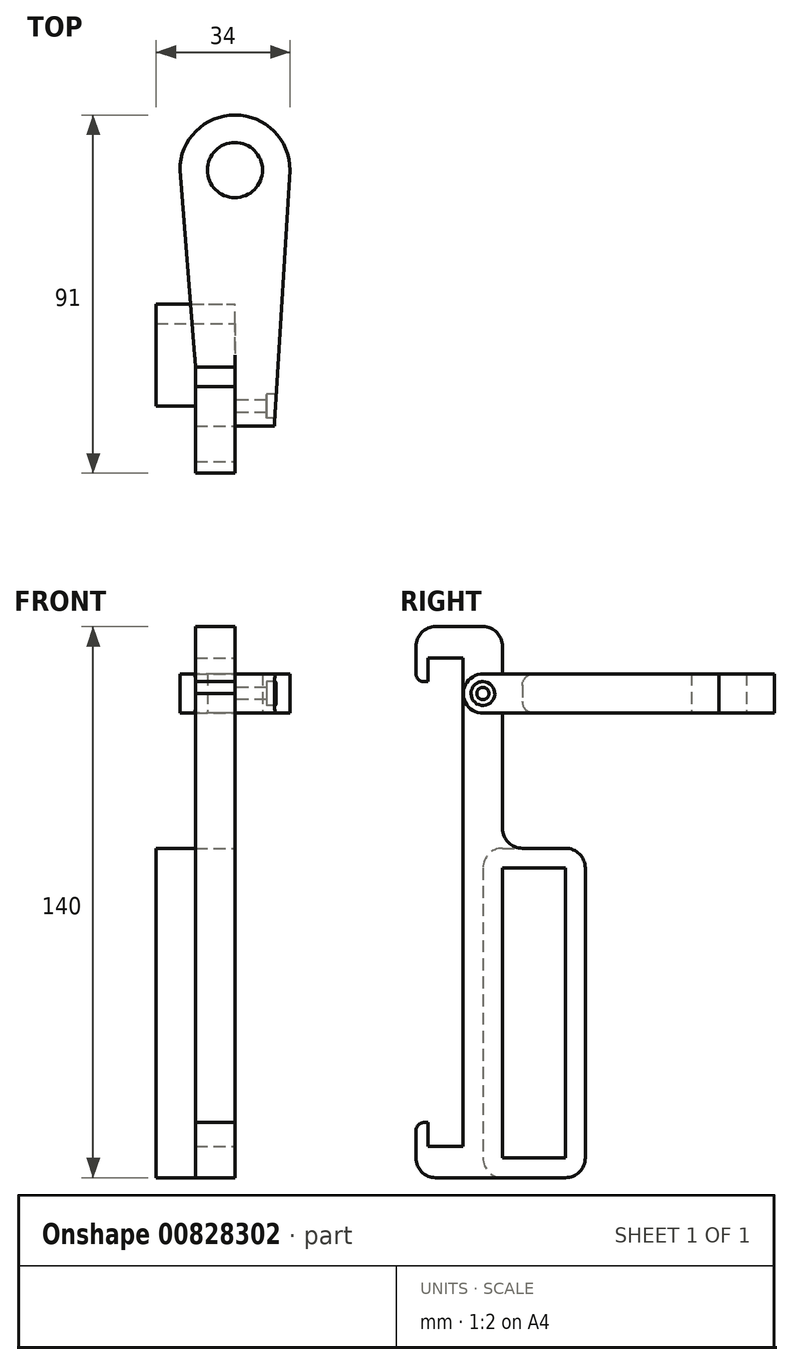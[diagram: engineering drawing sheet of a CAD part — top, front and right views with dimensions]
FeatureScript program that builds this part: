
annotation { "Feature Type Name" : "Feature", "Feature Type Description" : "" }
export const myFeature = defineFeature(function(context is Context, id is Id, definition is map)
    precondition{}
    {
        {
            var Q0;
            Q0=qCreatedBy(makeId("Top.planeOp"),FACE);
            var sketch = newSketch(context, id + "F0", { "sketchPlane" : qUnion([Q0])});
            skCircle(sketch, "E0", {"center": v(0, 0) * mm, "radius": 7 * mm});
            skArc(sketch, "E1", {"start": v(14, 0) * mm, "mid": v(0, 14) * mm, "end": v(-14, 0) * mm});
            skLineSegment(sketch, "E2", {"start": v(10, -65) * mm, "end": v(0, -65) * mm});
            skLineSegment(sketch, "E3", {"start": v(0, -65) * mm, "end": v(0, -50) * mm});
            skLineSegment(sketch, "E4", {"start": v(0, -50) * mm, "end": v(-10, -50) * mm});
            skLineSegment(sketch, "E5", {"start": v(-10, -50) * mm, "end": v(-14, 0) * mm});
            skLineSegment(sketch, "E6", {"start": v(0, 0) * mm, "end": v(0, -50) * mm, "construction": true});
            skLineSegment(sketch, "E7", {"start": v(14, 0) * mm, "end": v(10, -65) * mm});
            skSolve(sketch);
        }
        {
            var Q0;
            Q0 = qSketchRegion(id + "F0", true);
            extrude(context, id + "F1", {"entities" : qUnion([Q0]), "depth" : 10 * mm, "offsetDistance" : 25 * mm});
        }
        {
            var Q0;
            Q0=makeQuery(id+"F1.opExtrude","CAP_EDGE",EDGE,{"disambiguationData":[OSD([sQuery(id+"F0.wireOp",EDGE,"E2")])],"isStart":false});
            var Q1;
            Q1=makeQuery(id+"F1.opExtrude","CAP_EDGE",EDGE,{"disambiguationData":[OSD([sQuery(id+"F0.wireOp",EDGE,"E2")])],"isStart":true});
            fillet(context, id + "F2", {"entities" : qUnion([Q0, Q1]), "radius" : 5 * mm, "tangentPropagation" : true, "allowEdgeOverflow" : false});
        }
        {
            var Q0;
            Q0=makeQuery(id+"F1.opExtrude","SWEPT_FACE",FACE,{"disambiguationData":[OSD([sQuery(id+"F0.wireOp",EDGE,"E3")])]});
            var sketch = newSketch(context, id + "F3", { "sketchPlane" : qUnion([Q0])});
            skPoint(sketch, "E8", {"position": v(60, 0) * mm});
            skPoint(sketch, "E9", {"position": v(60, 10) * mm});
            skLineSegment(sketch, "E10", {"start": v(60, 0) * mm, "end": v(60, 10) * mm, "construction": true});
            skCircle(sketch, "E11", {"center": v(60, 5) * mm, "radius": 1.55 * mm});
            skCircle(sketch, "E12", {"center": v(60, 5) * mm, "radius": 3.05 * mm});
            skSolve(sketch);
        }
        {
            var Q0;
            Q0=makeQuery(id+"F3.imprint","IMPRINT",FACE,{"disambiguationData":[TD([[makeQuery(id+"F3.imprint","IMPRINT",EDGE,{"derivedFrom":sQuery(id+"F3.wireOp",EDGE,"E11")}),1.0]])]});
            var Q1;
            Q1=sQuery(id+"F3.wireOp",EDGE,"E11");
            var Q2;
            Q2=makeQuery(id+"F1.opExtrude","SWEPT_FACE",FACE,{"disambiguationData":[OSD([sQuery(id+"F0.wireOp",EDGE,"E7")])]});
            extrude(context, id + "F4", {"entities" : qUnion([Q0]), "operationType" : NewBodyOperationType.REMOVE, "surfaceEntities" : qUnion([Q1]), "endBound" : BoundingType.UP_TO_SURFACE, "oppositeDirection" : true, "depth" : 25 * mm, "endBoundEntityFace" : qUnion([Q2]), "offsetDistance" : 25 * mm});
        }
        {
            var Q0;
            Q0=makeQuery(id+"F3.imprint","IMPRINT",FACE,{"disambiguationData":[TD([[makeQuery(id+"F3.imprint","IMPRINT",EDGE,{"derivedFrom":sQuery(id+"F3.wireOp",EDGE,"E11")}),-1.0]])]});
            extrude(context, id + "F5", {"entities" : qUnion([Q0]), "operationType" : NewBodyOperationType.REMOVE, "oppositeDirection" : true, "depth" : 12 * mm, "offsetDistance" : 25 * mm, "hasSecondDirection" : true, "secondDirectionOppositeDirection" : true, "secondDirectionDepth" : 8 * mm});
        }
        {
            var Q0;
            Q0=makeQuery(id+"F1.opExtrude","SWEPT_FACE",FACE,{"disambiguationData":[OSD([sQuery(id+"F0.wireOp",EDGE,"E3")])]});
            var sketch = newSketch(context, id + "F6", { "sketchPlane" : qUnion([Q0])});
            skLineSegment(sketch, "E13", {"start": v(65, -110) * mm, "end": v(74, -110) * mm});
            skLineSegment(sketch, "E14", {"start": v(74, -110) * mm, "end": v(74, -104) * mm});
            skLineSegment(sketch, "E15", {"start": v(74, -104) * mm, "end": v(75, -104) * mm});
            skLineSegment(sketch, "E16", {"start": v(77, -106) * mm, "end": v(77, -113) * mm});
            skLineSegment(sketch, "E17", {"start": v(55, -110) * mm, "end": v(55, -113) * mm});
            skPoint(sketch, "E18.visualSharp", {"position": v(77, -118) * mm});
            skArc(sketch, "E18.filletArc", {"start": v(72, -118) * mm, "mid": v(75.54, -116.54) * mm, "end": v(77, -113) * mm});
            skPoint(sketch, "E19.visualSharp", {"position": v(77, -104) * mm});
            skArc(sketch, "E19.filletArc", {"start": v(77, -106) * mm, "mid": v(76.41, -104.59) * mm, "end": v(75, -104) * mm});
            skLineSegment(sketch, "E20", {"start": v(65, 14) * mm, "end": v(65, -110) * mm});
            skLineSegment(sketch, "E21", {"start": v(55, 14) * mm, "end": v(55, -29.3) * mm});
            skLineSegment(sketch, "E22", {"start": v(65, -48) * mm, "end": v(85, -48) * mm, "construction": true});
            skLineSegment(sketch, "E23.MirrorCS", {"start": v(65, 14) * mm, "end": v(74, 14) * mm});
            skLineSegment(sketch, "E24.MirrorCS", {"start": v(74, 14) * mm, "end": v(74, 8) * mm});
            skLineSegment(sketch, "E25.MirrorCS", {"start": v(74, 8) * mm, "end": v(75, 8) * mm});
            skArc(sketch, "E26.MirrorCS", {"start": v(77, 10) * mm, "mid": v(76.41, 8.59) * mm, "end": v(75, 8) * mm});
            skLineSegment(sketch, "E27.MirrorCS", {"start": v(77, 10) * mm, "end": v(77, 17) * mm});
            skArc(sketch, "E28.MirrorCS", {"start": v(72, 22) * mm, "mid": v(75.54, 20.54) * mm, "end": v(77, 17) * mm});
            skLineSegment(sketch, "E29.MirrorCS", {"start": v(72, 22) * mm, "end": v(60, 22) * mm});
            skArc(sketch, "E30.MirrorCS", {"start": v(55, 17) * mm, "mid": v(56.46, 20.54) * mm, "end": v(60, 22) * mm});
            skLineSegment(sketch, "E31.MirrorCS", {"start": v(55, 14) * mm, "end": v(55, 17) * mm});
            skLineSegment(sketch, "E32.bottom", {"start": v(55, -113) * mm, "end": v(39, -113) * mm});
            skLineSegment(sketch, "E32.top", {"start": v(55, -39.3) * mm, "end": v(39, -39.3) * mm});
            skLineSegment(sketch, "E32.left", {"start": v(55, -113) * mm, "end": v(55, -39.3) * mm});
            skLineSegment(sketch, "E32.right", {"start": v(39, -113) * mm, "end": v(39, -39.3) * mm});
            skLineSegment(sketch, "E33.1", {"start": v(34, -113) * mm, "end": v(34, -39.3) * mm});
            skLineSegment(sketch, "E33.2", {"start": v(50, -34.3) * mm, "end": v(39, -34.3) * mm});
            skLineSegment(sketch, "E34.trimOffspring", {"start": v(55, -39.3) * mm, "end": v(55, -110) * mm});
            skLineSegment(sketch, "E35", {"start": v(39, -118) * mm, "end": v(72, -118) * mm});
            skPoint(sketch, "E36.visualSharp", {"position": v(34, -118) * mm});
            skArc(sketch, "E36.filletArc", {"start": v(34, -113) * mm, "mid": v(35.46, -116.54) * mm, "end": v(39, -118) * mm});
            skPoint(sketch, "E37.visualSharp", {"position": v(34, -34.3) * mm});
            skArc(sketch, "E37.filletArc", {"start": v(39, -34.3) * mm, "mid": v(35.46, -35.76) * mm, "end": v(34, -39.3) * mm});
            skPoint(sketch, "E38.visualSharp", {"position": v(55, -34.3) * mm});
            skArc(sketch, "E38.filletArc", {"start": v(50, -34.3) * mm, "mid": v(53.54, -32.84) * mm, "end": v(55, -29.3) * mm});
            skSolve(sketch);
        }
        {
            var Q0;
            Q0=makeQuery(id+"F6.imprint","IMPRINT",FACE,{"disambiguationData":[TD([[makeQuery(id+"F6.imprint","IMPRINT",EDGE,{"derivedFrom":makeQuery(id+"F4.boolean.opBoolean","COPY",EDGE,{"derivedFrom":makeQuery(id+"F4.opExtrude","CAP_EDGE",EDGE,{"disambiguationData":[OSD([sQuery(id+"F3.wireOp",EDGE,"E11")])],"isStart":true})})}),-1.0]])]});
            var Q1;
            {var subQ7=sQuery(id+"F6.wireOp",EDGE,"0UclWwWG-CQ9r-8rmC-3t0o-oFOVJa3uRY5Y");Q1=makeQuery(id+"F6.imprint","IMPRINT",FACE,{"disambiguationData":[TD([[makeQuery(id+"F6.imprint","IMPRINT",EDGE,{"derivedFrom":subQ7}),1.0]])]});}
            var Q2;
            {var subQ8=sQuery(id+"F6.wireOp",EDGE,"E13");Q2=makeQuery(id+"F6.imprint","IMPRINT",FACE,{"disambiguationData":[TD([[makeQuery(id+"F6.imprint","IMPRINT",EDGE,{"derivedFrom":subQ8}),-1.0]])]});}
            var Q3;
            Q3=makeQuery(id+"F6.imprint","IMPRINT",FACE,{"disambiguationData":[TD([[makeQuery(id+"F6.imprint","IMPRINT",EDGE,{"derivedFrom":sQuery(id+"F6.wireOp",EDGE,"0UclWwWG-CQ9r-8rmC-3t0o-oFOVJa3uRY5Y")}),-1.0]])]});
            var Q4;
            {var subQ6=sQuery(id+"F6.wireOp",EDGE,"E23.MirrorCS");Q4=makeQuery(id+"F6.imprint","IMPRINT",FACE,{"disambiguationData":[TD([[makeQuery(id+"F6.imprint","IMPRINT",EDGE,{"derivedFrom":subQ6}),1.0]])]});}
            extrude(context, id + "F7", {"entities" : qUnion([Q0, Q1, Q2, Q3, Q4]), "depth" : 10 * mm, "offsetDistance" : 25 * mm});
        }
        {
            var Q0;
            Q0=makeQuery(id+"F7.opExtrude","CAP_FACE",FACE,{"disambiguationData":[OSD([sQuery(id+"F3.wireOp",EDGE,"E11"),sQuery(id+"F6.wireOp",EDGE,"bUPbGr09-necb-y4z6-tEju-2VODjiAXuSOo.left"),sQuery(id+"F6.wireOp",EDGE,"bUPbGr09-necb-y4z6-tEju-2VODjiAXuSOo.right"),sQuery(id+"F6.wireOp",EDGE,"55dd8d40-e183-4ee7-96f7-8d9655a16e07.filletArc"),sQuery(id+"F6.wireOp",EDGE,"86c6cade-5d1c-4868-ab3d-ae4e29603d97.filletArc"),sQuery(id+"F6.wireOp",EDGE,"E13"),sQuery(id+"F6.wireOp",EDGE,"E14"),sQuery(id+"F6.wireOp",EDGE,"E15"),sQuery(id+"F6.wireOp",EDGE,"E16"),sQuery(id+"F6.wireOp",EDGE,"E17"),sQuery(id+"F6.wireOp",EDGE,"JK7yhdwg-f7QC-nTv9-UEI6-wTwSWF0jWrCr"),sQuery(id+"F6.wireOp",EDGE,"5c3730f8-11a7-420e-9a6c-b66555e10253.filletArc"),sQuery(id+"F6.wireOp",EDGE,"E18.filletArc"),sQuery(id+"F6.wireOp",EDGE,"E19.filletArc")])],"isStart":false});
            var sketch = newSketch(context, id + "F8", { "sketchPlane" : qUnion([Q0])});
            skCircle(sketch, "E39.cCircle", {"center": v(60, 5) * mm, "radius": 2.8 * mm, "construction": true});
            skLineSegment(sketch, "E39.0", {"start": v(62.8, 6.62) * mm, "end": v(62.8, 3.38) * mm});
            skLineSegment(sketch, "E39.1", {"start": v(62.8, 3.38) * mm, "end": v(60, 1.77) * mm});
            skLineSegment(sketch, "E39.2", {"start": v(60, 1.77) * mm, "end": v(57.2, 3.38) * mm});
            skLineSegment(sketch, "E39.3", {"start": v(57.2, 3.38) * mm, "end": v(57.2, 6.62) * mm});
            skLineSegment(sketch, "E39.4", {"start": v(57.2, 6.62) * mm, "end": v(60, 8.23) * mm});
            skLineSegment(sketch, "E39.5", {"start": v(60, 8.23) * mm, "end": v(62.8, 6.62) * mm});
            skPoint(sketch, "E39.0.midPoint", {"position": v(62.8, 5) * mm});
            skSolve(sketch);
        }
        {
            var Q0;
            Q0=makeQuery(id+"F8.imprint","IMPRINT",FACE,{"disambiguationData":[TD([[makeQuery(id+"F8.imprint","IMPRINT",EDGE,{"derivedFrom":sQuery(id+"F8.wireOp",EDGE,"E39.0")}),-1.0]])]});
            extrude(context, id + "F9", {"entities" : qUnion([Q0]), "operationType" : NewBodyOperationType.REMOVE, "oppositeDirection" : true, "depth" : 2 * mm, "offsetDistance" : 25 * mm});
        }
        {
            var Q0;
            Q0=makeQuery(id+"F1.opExtrude","CAP_EDGE",EDGE,{"disambiguationData":[OSD([sQuery(id+"F0.wireOp",EDGE,"E4")])],"isStart":false});
            var Q1;
            Q1=makeQuery(id+"F1.opExtrude","CAP_EDGE",EDGE,{"disambiguationData":[OSD([sQuery(id+"F0.wireOp",EDGE,"E4")])],"isStart":true});
            fillet(context, id + "F10", {"entities" : qUnion([Q0, Q1]), "radius" : 3 * mm, "tangentPropagation" : true, "allowEdgeOverflow" : false});
        }
        {
            var Q0;
            Q0=makeQuery(id+"F7.opExtrude","CAP_FACE",FACE,{"disambiguationData":[OSD([sQuery(id+"F3.wireOp",EDGE,"E11"),sQuery(id+"F6.wireOp",EDGE,"E13"),sQuery(id+"F6.wireOp",EDGE,"E14"),sQuery(id+"F6.wireOp",EDGE,"E15"),sQuery(id+"F6.wireOp",EDGE,"E16"),sQuery(id+"F6.wireOp",EDGE,"E18.filletArc"),sQuery(id+"F6.wireOp",EDGE,"E19.filletArc"),sQuery(id+"F6.wireOp",EDGE,"E20"),sQuery(id+"F6.wireOp",EDGE,"E21"),sQuery(id+"F6.wireOp",EDGE,"E23.MirrorCS"),sQuery(id+"F6.wireOp",EDGE,"E24.MirrorCS"),sQuery(id+"F6.wireOp",EDGE,"E25.MirrorCS"),sQuery(id+"F6.wireOp",EDGE,"E26.MirrorCS"),sQuery(id+"F6.wireOp",EDGE,"E27.MirrorCS"),sQuery(id+"F6.wireOp",EDGE,"E28.MirrorCS"),sQuery(id+"F6.wireOp",EDGE,"E29.MirrorCS"),sQuery(id+"F6.wireOp",EDGE,"E30.MirrorCS"),sQuery(id+"F6.wireOp",EDGE,"E31.MirrorCS"),sQuery(id+"F6.wireOp",EDGE,"E32.bottom"),sQuery(id+"F6.wireOp",EDGE,"E32.top"),sQuery(id+"F6.wireOp",EDGE,"E32.left"),sQuery(id+"F6.wireOp",EDGE,"E32.right"),sQuery(id+"F6.wireOp",EDGE,"E33.1"),sQuery(id+"F6.wireOp",EDGE,"E33.2"),sQuery(id+"F6.wireOp",EDGE,"E34.trimOffspring"),sQuery(id+"F6.wireOp",EDGE,"E35"),sQuery(id+"F6.wireOp",EDGE,"E36.filletArc"),sQuery(id+"F6.wireOp",EDGE,"E37.filletArc"),sQuery(id+"F6.wireOp",EDGE,"E38.filletArc")])],"isStart":false});
            var sketch = newSketch(context, id + "F11", { "sketchPlane" : qUnion([Q0])});
            skLineSegment(sketch, "E40.0", {"start": v(39, -113) * mm, "end": v(39, -39.3) * mm});
            skLineSegment(sketch, "E40.1", {"start": v(55, -113) * mm, "end": v(39, -113) * mm});
            skLineSegment(sketch, "E40.2", {"start": v(55, -39.3) * mm, "end": v(55, -113) * mm});
            skLineSegment(sketch, "E40.3", {"start": v(55, -39.3) * mm, "end": v(39, -39.3) * mm});
            skLineSegment(sketch, "E41.0", {"start": v(34, -113) * mm, "end": v(34, -39.3) * mm});
            skLineSegment(sketch, "E41.1", {"start": v(55, -118) * mm, "end": v(39, -118) * mm});
            skLineSegment(sketch, "E41.2", {"start": v(60, -39.3) * mm, "end": v(60, -113) * mm});
            skLineSegment(sketch, "E41.3", {"start": v(55, -34.3) * mm, "end": v(39, -34.3) * mm});
            skPoint(sketch, "E42.visualSharp", {"position": v(34, -34.3) * mm});
            skArc(sketch, "E42.filletArc", {"start": v(39, -34.3) * mm, "mid": v(35.46, -35.76) * mm, "end": v(34, -39.3) * mm});
            skPoint(sketch, "E43.visualSharp", {"position": v(60, -34.3) * mm});
            skArc(sketch, "E43.filletArc", {"start": v(60, -39.3) * mm, "mid": v(58.54, -35.76) * mm, "end": v(55, -34.3) * mm});
            skPoint(sketch, "E44.visualSharp", {"position": v(34, -118) * mm});
            skArc(sketch, "E44.filletArc", {"start": v(34, -113) * mm, "mid": v(35.46, -116.54) * mm, "end": v(39, -118) * mm});
            skPoint(sketch, "E45.visualSharp", {"position": v(60, -118) * mm});
            skArc(sketch, "E45.filletArc", {"start": v(55, -118) * mm, "mid": v(58.54, -116.54) * mm, "end": v(60, -113) * mm});
            skSolve(sketch);
        }
        {
            var Q0;
            Q0=makeQuery(id+"F11.imprint","IMPRINT",FACE,{"disambiguationData":[TD([[makeQuery(id+"F11.imprint","IMPRINT",EDGE,{"derivedFrom":sQuery(id+"F11.wireOp",EDGE,"E40.0")}),1.0]])]});
            extrude(context, id + "F12", {"entities" : qUnion([Q0]), "operationType" : NewBodyOperationType.ADD, "depth" : 10 * mm, "offsetDistance" : 25 * mm});
        }
    });
